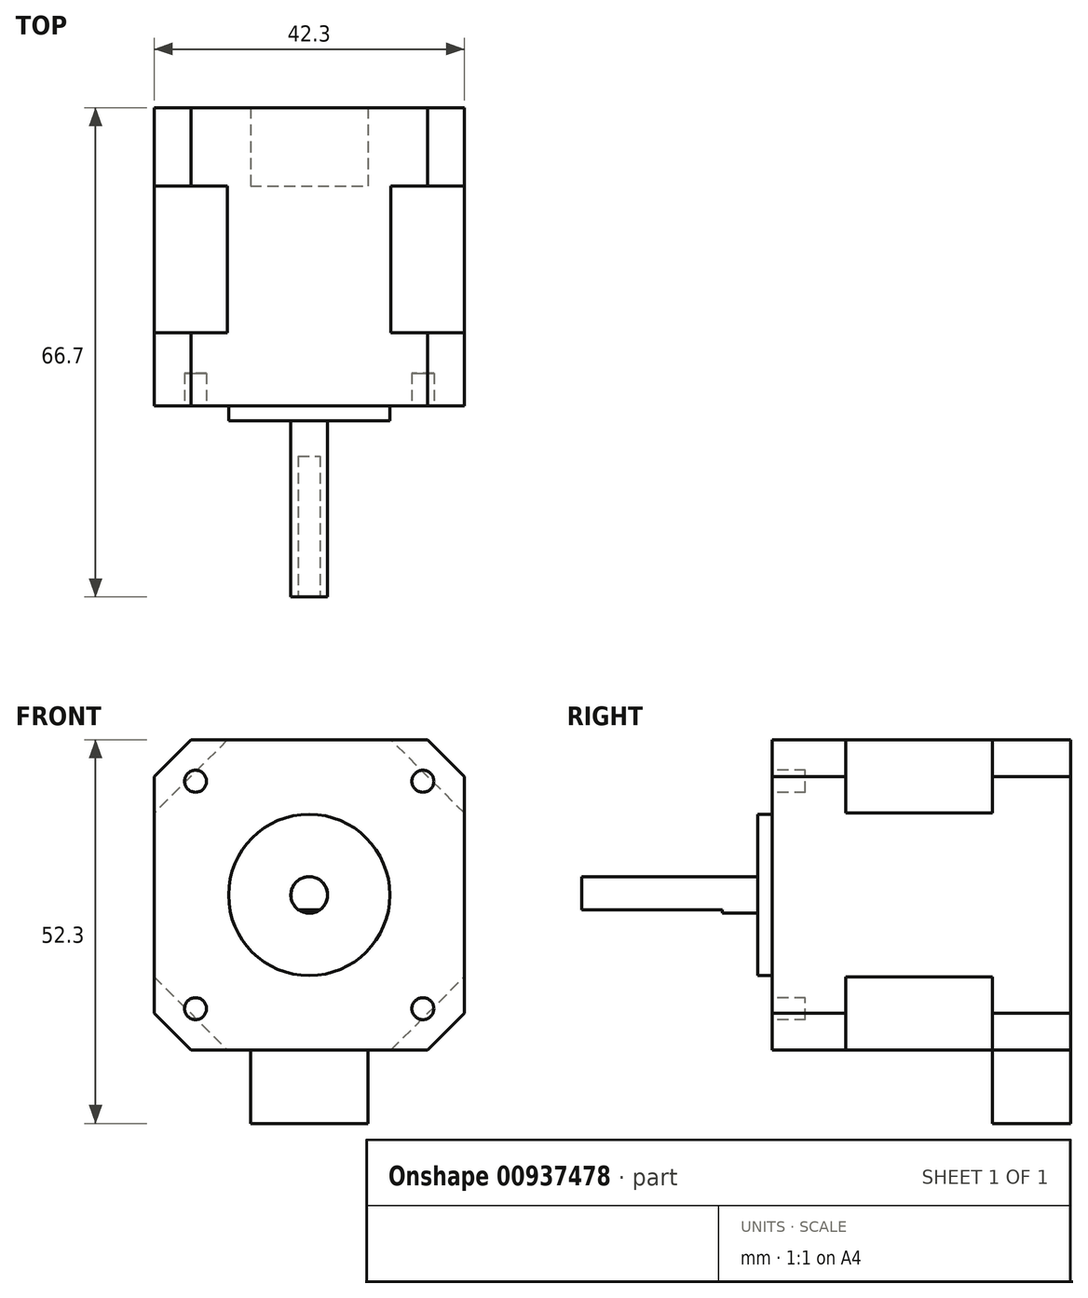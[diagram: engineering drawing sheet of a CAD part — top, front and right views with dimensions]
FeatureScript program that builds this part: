
annotation { "Feature Type Name" : "Feature", "Feature Type Description" : "" }
export const myFeature = defineFeature(function(context is Context, id is Id, definition is map)
    precondition{}
    {
        {
            var Q0;
            Q0=qCreatedBy(makeId("Front.planeOp"),FACE);
            var sketch = newSketch(context, id + "F0", { "sketchPlane" : qUnion([Q0])});
            skLineSegment(sketch, "E0.0", {"start": v(-11.15, 21.15) * mm, "end": v(-21.15, 11.15) * mm});
            skLineSegment(sketch, "E0.1", {"start": v(-21.15, 16.15) * mm, "end": v(-16.15, 21.15) * mm});
            skLineSegment(sketch, "E0.2", {"start": v(-21.15, -11.15) * mm, "end": v(-11.15, -21.15) * mm});
            skLineSegment(sketch, "E0.3", {"start": v(-16.15, -21.15) * mm, "end": v(-21.15, -16.15) * mm});
            skLineSegment(sketch, "E0.4", {"start": v(11.15, -21.15) * mm, "end": v(21.15, -11.15) * mm});
            skLineSegment(sketch, "E0.5", {"start": v(21.15, -16.15) * mm, "end": v(16.15, -21.15) * mm});
            skLineSegment(sketch, "E0.6", {"start": v(21.15, 11.15) * mm, "end": v(11.15, 21.15) * mm});
            skLineSegment(sketch, "E0.7", {"start": v(16.15, 21.15) * mm, "end": v(21.15, 16.15) * mm});
            skLineSegment(sketch, "E1", {"start": v(-21.15, 16.15) * mm, "end": v(-21.15, -16.15) * mm});
            skLineSegment(sketch, "E2", {"start": v(-16.15, -21.15) * mm, "end": v(16.15, -21.15) * mm});
            skLineSegment(sketch, "E3", {"start": v(21.15, -16.15) * mm, "end": v(21.15, 16.15) * mm});
            skLineSegment(sketch, "E4", {"start": v(16.15, 21.15) * mm, "end": v(-16.15, 21.15) * mm});
            skLineSegment(sketch, "E5", {"start": v(0, -31.15) * mm, "end": v(8, -31.15) * mm});
            skPoint(sketch, "E5.startSnap0", {"position": v(0, -21.15) * mm});
            skLineSegment(sketch, "E6", {"start": v(8, -31.15) * mm, "end": v(8, -21.15) * mm});
            skLineSegment(sketch, "E7", {"start": v(0, -31.15) * mm, "end": v(-8, -31.15) * mm});
            skLineSegment(sketch, "E8", {"start": v(-8, -31.15) * mm, "end": v(-8, -21.15) * mm});
            skLineSegment(sketch, "E9", {"start": v(-18.65, 18.65) * mm, "end": v(18.65, -18.65) * mm, "construction": true});
            skLineSegment(sketch, "E10", {"start": v(-18.65, -18.65) * mm, "end": v(18.65, 18.65) * mm, "construction": true});
            skPoint(sketch, "E11", {"position": v(0, 0) * mm});
            skSolve(sketch);
        }
        {
            var Q0;
            {var subQ0=sQuery(id+"F0.wireOp",EDGE,"E0.0");Q0=makeQuery(id+"F0.imprint","IMPRINT",FACE,{"disambiguationData":[TD([[makeQuery(id+"F0.imprint","IMPRINT",EDGE,{"derivedFrom":subQ0}),-1.0]])]});}
            var Q1;
            {var subQ0=sQuery(id+"F0.wireOp",EDGE,"E0.2");Q1=makeQuery(id+"F0.imprint","IMPRINT",FACE,{"disambiguationData":[TD([[makeQuery(id+"F0.imprint","IMPRINT",EDGE,{"derivedFrom":subQ0}),-1.0]])]});}
            var Q2;
            {var subQ0=sQuery(id+"F0.wireOp",EDGE,"E0.4");Q2=makeQuery(id+"F0.imprint","IMPRINT",FACE,{"disambiguationData":[TD([[makeQuery(id+"F0.imprint","IMPRINT",EDGE,{"derivedFrom":subQ0}),-1.0]])]});}
            var Q3;
            {var subQ0=sQuery(id+"F0.wireOp",EDGE,"E0.6");Q3=makeQuery(id+"F0.imprint","IMPRINT",FACE,{"disambiguationData":[TD([[makeQuery(id+"F0.imprint","IMPRINT",EDGE,{"derivedFrom":subQ0}),-1.0]])]});}
            var Q4;
            {var subQ7=sQuery(id+"F0.wireOp",EDGE,"E0.0");Q4=makeQuery(id+"F0.imprint","IMPRINT",FACE,{"disambiguationData":[TD([[makeQuery(id+"F0.imprint","IMPRINT",EDGE,{"derivedFrom":subQ7}),1.0]])]});}
            extrude(context, id + "F1", {"entities" : qUnion([Q0, Q1, Q2, Q3, Q4]), "depth" : 10 * mm, "offsetDistance" : 25 * mm});
        }
        {
            var Q0;
            Q0 = qSketchRegion(id + "F0", true);
            extrude(context, id + "F2", {"entities" : qUnion([Q0]), "operationType" : NewBodyOperationType.ADD, "oppositeDirection" : true, "depth" : 30.7 * mm, "offsetDistance" : 25 * mm});
        }
        {
            var Q0;
            {var subQ0=sQuery(id+"F0.wireOp",EDGE,"E0.6");Q0=makeQuery(id+"F0.imprint","IMPRINT",FACE,{"disambiguationData":[TD([[makeQuery(id+"F0.imprint","IMPRINT",EDGE,{"derivedFrom":subQ0}),-1.0]])]});}
            var Q1;
            {var subQ0=sQuery(id+"F0.wireOp",EDGE,"E0.0");Q1=makeQuery(id+"F0.imprint","IMPRINT",FACE,{"disambiguationData":[TD([[makeQuery(id+"F0.imprint","IMPRINT",EDGE,{"derivedFrom":subQ0}),-1.0]])]});}
            var Q2;
            {var subQ0=sQuery(id+"F0.wireOp",EDGE,"E0.2");Q2=makeQuery(id+"F0.imprint","IMPRINT",FACE,{"disambiguationData":[TD([[makeQuery(id+"F0.imprint","IMPRINT",EDGE,{"derivedFrom":subQ0}),-1.0]])]});}
            var Q3;
            {var subQ0=sQuery(id+"F0.wireOp",EDGE,"E0.4");Q3=makeQuery(id+"F0.imprint","IMPRINT",FACE,{"disambiguationData":[TD([[makeQuery(id+"F0.imprint","IMPRINT",EDGE,{"derivedFrom":subQ0}),-1.0]])]});}
            var Q4;
            Q4=makeQuery(id+"F0.imprint","IMPRINT",FACE,{"disambiguationData":[TD([[makeQuery(id+"F0.imprint","IMPRINT",EDGE,{"derivedFrom":sQuery(id+"F0.wireOp",EDGE,"E5")}),1.0]])]});
            extrude(context, id + "F3", {"entities" : qUnion([Q0, Q1, Q2, Q3, Q4]), "operationType" : NewBodyOperationType.REMOVE, "oppositeDirection" : true, "depth" : 20 * mm, "offsetDistance" : 25 * mm});
        }
        {
            var Q0;
            Q0=makeQuery(id+"F1.opExtrude","CAP_FACE",FACE,{"disambiguationData":[OSD([sQuery(id+"F0.wireOp",EDGE,"E0.1"),sQuery(id+"F0.wireOp",EDGE,"E0.3"),sQuery(id+"F0.wireOp",EDGE,"E0.5"),sQuery(id+"F0.wireOp",EDGE,"E0.7"),sQuery(id+"F0.wireOp",EDGE,"E1"),sQuery(id+"F0.wireOp",EDGE,"E2"),sQuery(id+"F0.wireOp",EDGE,"E3"),sQuery(id+"F0.wireOp",EDGE,"E4")])],"isStart":false});
            var sketch = newSketch(context, id + "F4", { "sketchPlane" : qUnion([Q0])});
            skCircle(sketch, "E12", {"center": v(0, 0) * mm, "radius": 11 * mm});
            skCircle(sketch, "E13", {"center": v(0, 0) * mm, "radius": 2.5 * mm});
            skCircle(sketch, "E14.0", {"center": v(-15.5, 15.5) * mm, "radius": 1.5 * mm});
            skCircle(sketch, "E14.1", {"center": v(-15.5, -15.5) * mm, "radius": 1.5 * mm});
            skCircle(sketch, "E14.3", {"center": v(15.5, 15.5) * mm, "radius": 1.5 * mm});
            skCircle(sketch, "E14.4", {"center": v(15.5, -15.5) * mm, "radius": 1.5 * mm});
            skSolve(sketch);
        }
        {
            var Q0;
            Q0=makeQuery(id+"F4.imprint","IMPRINT",FACE,{"disambiguationData":[TD([[makeQuery(id+"F4.imprint","IMPRINT",EDGE,{"derivedFrom":sQuery(id+"F4.wireOp",EDGE,"E12")}),1.0]])]});
            extrude(context, id + "F5", {"entities" : qUnion([Q0]), "operationType" : NewBodyOperationType.ADD, "depth" : 2 * mm, "offsetDistance" : 25 * mm});
        }
        {
            var Q0;
            Q0=makeQuery(id+"F4.imprint","IMPRINT",FACE,{"disambiguationData":[TD([[makeQuery(id+"F4.imprint","IMPRINT",EDGE,{"derivedFrom":sQuery(id+"F4.wireOp",EDGE,"E13")}),1.0]])]});
            extrude(context, id + "F6", {"entities" : qUnion([Q0]), "operationType" : NewBodyOperationType.ADD, "depth" : 26 * mm, "offsetDistance" : 25 * mm});
        }
        {
            var Q0;
            Q0=makeQuery(id+"F6.opExtrude","CAP_FACE",FACE,{"disambiguationData":[OSD([sQuery(id+"F4.wireOp",EDGE,"E13")])],"isStart":false});
            var sketch = newSketch(context, id + "F7", { "sketchPlane" : qUnion([Q0])});
            skCircle(sketch, "E15.0", {"center": v(0, 0) * mm, "radius": 2.5 * mm});
            skLineSegment(sketch, "E16", {"start": v(-1.5, -2) * mm, "end": v(1.5, -2) * mm});
            skLineSegment(sketch, "E17", {"start": v(0, -2) * mm, "end": v(0, 2.5) * mm, "construction": true});
            skSolve(sketch);
        }
        {
            var Q0;
            {var subQ0=sQuery(id+"F7.wireOp",EDGE,"E16");Q0=makeQuery(id+"F7.imprint","IMPRINT",FACE,{"disambiguationData":[TD([[makeQuery(id+"F7.imprint","IMPRINT",EDGE,{"derivedFrom":subQ0}),-1.0]])]});}
            extrude(context, id + "F8", {"entities" : qUnion([Q0]), "operationType" : NewBodyOperationType.REMOVE, "oppositeDirection" : true, "depth" : 19.2 * mm, "offsetDistance" : 25 * mm});
        }
        {
            var Q0;
            Q0=makeQuery(id+"F4.imprint","IMPRINT",FACE,{"disambiguationData":[TD([[makeQuery(id+"F4.imprint","IMPRINT",EDGE,{"derivedFrom":sQuery(id+"F4.wireOp",EDGE,"E14.0")}),1.0]])]});
            var Q1;
            Q1=makeQuery(id+"F4.imprint","IMPRINT",FACE,{"disambiguationData":[TD([[makeQuery(id+"F4.imprint","IMPRINT",EDGE,{"derivedFrom":sQuery(id+"F4.wireOp",EDGE,"E14.3")}),1.0]])]});
            var Q2;
            Q2=makeQuery(id+"F4.imprint","IMPRINT",FACE,{"disambiguationData":[TD([[makeQuery(id+"F4.imprint","IMPRINT",EDGE,{"derivedFrom":sQuery(id+"F4.wireOp",EDGE,"E14.4")}),1.0]])]});
            var Q3;
            Q3=makeQuery(id+"F4.imprint","IMPRINT",FACE,{"disambiguationData":[TD([[makeQuery(id+"F4.imprint","IMPRINT",EDGE,{"derivedFrom":sQuery(id+"F4.wireOp",EDGE,"E14.1")}),1.0]])]});
            extrude(context, id + "F9", {"entities" : qUnion([Q0, Q1, Q2, Q3]), "operationType" : NewBodyOperationType.REMOVE, "oppositeDirection" : true, "depth" : 4.5 * mm, "offsetDistance" : 25 * mm});
        }
    });
